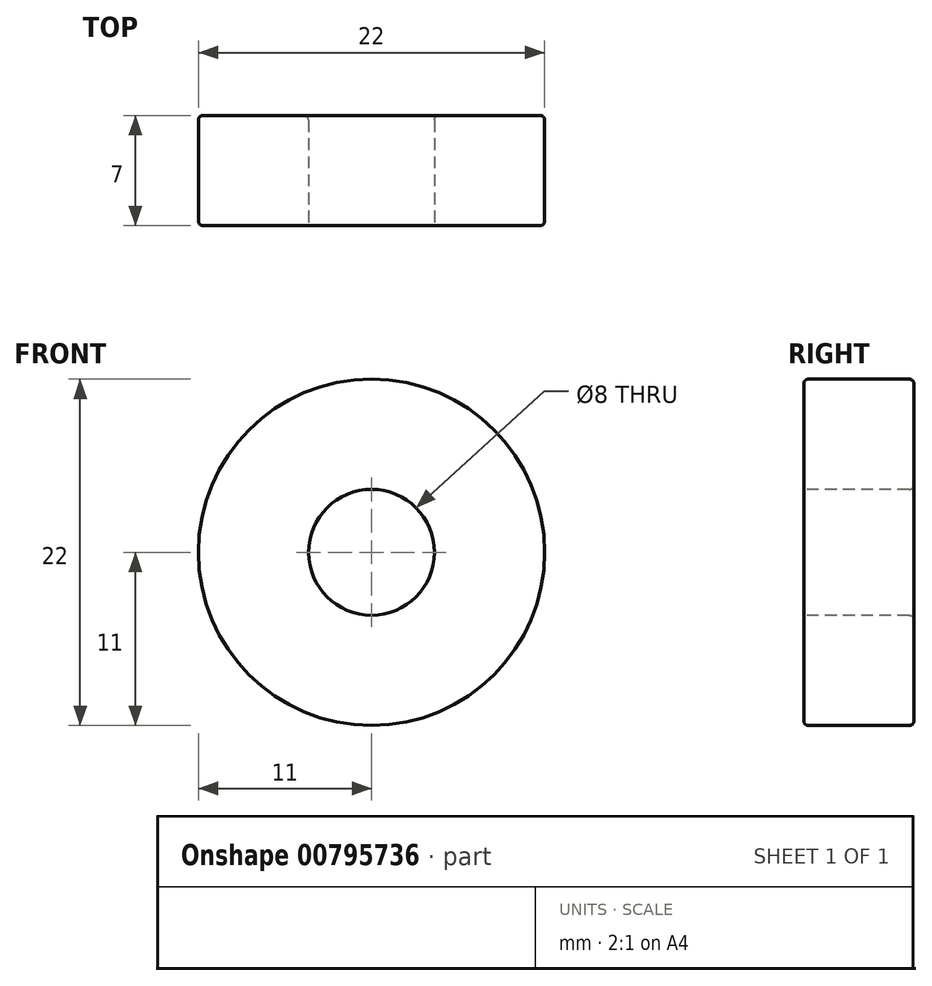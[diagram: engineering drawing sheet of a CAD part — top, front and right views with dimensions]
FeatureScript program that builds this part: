
annotation { "Feature Type Name" : "Feature", "Feature Type Description" : "" }
export const myFeature = defineFeature(function(context is Context, id is Id, definition is map)
    precondition{}
    {
        {
            var Q0;
            Q0=qCreatedBy(makeId("Front.planeOp"),FACE);
            var sketch = newSketch(context, id + "F0", { "sketchPlane" : qUnion([Q0])});
            skCircle(sketch, "E0", {"center": v(0, 0) * mm, "radius": 11 * mm});
            skSolve(sketch);
        }
        {
            var Q0;
            Q0 = qSketchRegion(id + "F0", true);
            extrude(context, id + "F1", {"entities" : qUnion([Q0]), "depth" : 7 * mm, "offsetDistance" : 25 * mm});
        }
        {
            var Q0;
            Q0=makeQuery(id+"F1.opExtrude","CAP_FACE",FACE,{"disambiguationData":[OSD([sQuery(id+"F0.wireOp",EDGE,"E0")])],"isStart":false});
            var sketch = newSketch(context, id + "F2", { "sketchPlane" : qUnion([Q0])});
            skCircle(sketch, "E1", {"center": v(0, 0) * mm, "radius": 4 * mm});
            skSolve(sketch);
        }
        {
            var Q0;
            Q0=makeQuery(id+"F2.imprint","IMPRINT",FACE,{"disambiguationData":[TD([[makeQuery(id+"F2.imprint","IMPRINT",EDGE,{"derivedFrom":sQuery(id+"F2.wireOp",EDGE,"E1")}),1.0]])]});
            extrude(context, id + "F3", {"entities" : qUnion([Q0]), "operationType" : NewBodyOperationType.REMOVE, "oppositeDirection" : true, "depth" : 25 * mm, "offsetDistance" : 25 * mm});
        }
        {
            var Q0;
            Q0=makeQuery(id+"F1.opExtrude","CAP_EDGE",EDGE,{"disambiguationData":[OSD([sQuery(id+"F0.wireOp",EDGE,"E0")])],"isStart":false});
            var Q1;
            Q1=makeQuery(id+"F1.opExtrude","CAP_EDGE",EDGE,{"disambiguationData":[OSD([sQuery(id+"F0.wireOp",EDGE,"E0")])],"isStart":true});
            var Q2;
            Q2=makeQuery(id+"F3.boolean.opBoolean","INTERSECT",EDGE,{"derivedFrom":[makeQuery(id+"F1.opExtrude","CAP_FACE",FACE,{"disambiguationData":[OSD([sQuery(id+"F0.wireOp",EDGE,"E0")])],"isStart":true}),makeQuery(id+"F3.opExtrude","SWEPT_FACE",FACE,{"disambiguationData":[OSD([sQuery(id+"F2.wireOp",EDGE,"E1")])]})]});
            var Q3;
            Q3=makeQuery(id+"F3.boolean.opBoolean","COPY",EDGE,{"derivedFrom":makeQuery(id+"F3.opExtrude","CAP_EDGE",EDGE,{"disambiguationData":[OSD([sQuery(id+"F2.wireOp",EDGE,"E1")])],"isStart":true})});
            fillet(context, id + "F4", {"entities" : qUnion([Q0, Q1, Q2, Q3]), "radius" : 0.3 * mm, "tangentPropagation" : true, "allowEdgeOverflow" : false});
        }
    });
